# Revit family: FU_Inspec_Atlas_Air_1-4
name_source: partatom
category: Furniture
units: mm (PartAtom-declared; Revit-internal decimal feet)

## family parameters
Always vertical = Yes
Cut with Voids When Loaded = No
OmniClass Number = 23.40.20.00
OmniClass Title = General Furniture and Specialties
Room Calculation Point = No
Shared = No
Work Plane-Based = No

## types (5) — shared parameters
Assembly Code = E2020
Depth = 660 mm  [stored 2.16535 ft]
Height = 100 mm  [stored 0.328084 ft]
Keynote = 46.B
Manufacturer = Inspec
Seat Pad Material = Leather - Rustical - Black
URL = https://inspecfurniture.com
Weight = 10.4
Width = 660 mm  [stored 2.16535 ft]
zero-valued in all types: Default Elevation

## per-type parameters (varying)
| type | Armrest Material | Description | Frame Material | Material_temp | Model | Seat Material |
| Atlas Air 2.3 Black w Grey Seat | Metal - Black - Matte | Armchair with 5-feet frame of cast recycled aluminum, casters as standard. Seat shell in mesh with flocked surface. | Metal - Black - Matte | Fabric - Grey Mesh | atlas air 2.3 | Fabric - Grey Mesh |
| Atlas Air 2.3 Chrome w White Seat | Metal - Chrome - Polished | Armchair with 5-feet frame of cast recycled aluminum, casters as standard. Seat shell in mesh with flocked surface. | Metal - Chrome - Polished | Fabric - White Mesh | atlas air 2.3 | Fabric - White Mesh |
| Atlas Air 2.4 Chrome w Black Seat | Metal - Chrome - Polished | Armchair with 5-feet frame of cast recycled aluminum, casters as standard. Seat shell in mesh with flocked surface. | Metal - Chrome - Polished | Fabric - Black Mesh | atlas air 2.4 | Fabric - Black Mesh |
| Atlas Air 1.4 Chrome w Black Seat | Metal - Chrome - Polished | Chair with 5-feet frame of cast recycled aluminum, casters as standard. Upholstered seat with shell in mesh with flocked surface. | Metal - Chrome - Polished | Fabric - Black Mesh | atlas air 1.4 | Fabric - Black Mesh |
| Atlas Air 1.3 Black w Rust Seat | Metal - Black - Matte | Chair with 5-feet frame of cast recycled aluminum, casters as standard. Seat shell in mesh with flocked surface. | Metal - Black - Matte | Fabric - Rust Mesh | atlas air 1.3 | Fabric - Rust Mesh |

note: [stored X ft] marks values corroborated as IEEE doubles in the binary element streams (Revit-internal decimal feet)

## geometry (parser evidence)
native form markers: Blend x8, Sweep x2
no freeform markers — native parametric forms only
